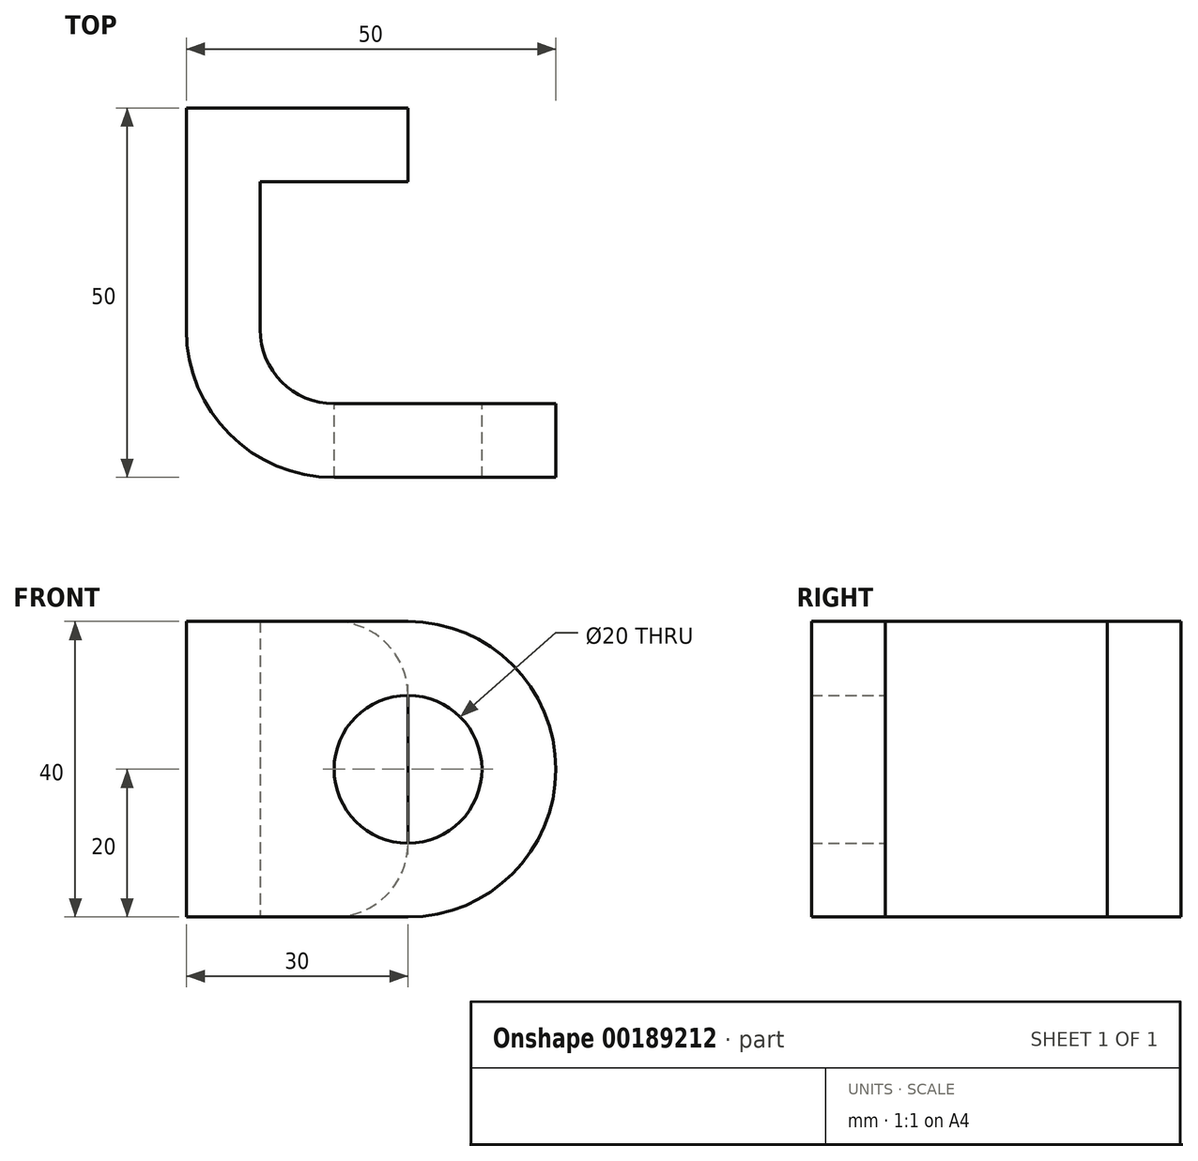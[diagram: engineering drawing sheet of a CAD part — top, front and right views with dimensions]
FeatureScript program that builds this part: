
annotation { "Feature Type Name" : "Feature", "Feature Type Description" : "" }
export const myFeature = defineFeature(function(context is Context, id is Id, definition is map)
    precondition{}
    {
        {
            var Q0;
            Q0=qCreatedBy(makeId("Top.planeOp"),FACE);
            var sketch = newSketch(context, id + "F0", { "sketchPlane" : qUnion([Q0])});
            skLineSegment(sketch, "E0", {"start": v(0, 10) * mm, "end": v(0, 30) * mm});
            skLineSegment(sketch, "E1", {"start": v(0, 30) * mm, "end": v(20, 30) * mm});
            skLineSegment(sketch, "E2", {"start": v(20, 30) * mm, "end": v(20, 40) * mm});
            skLineSegment(sketch, "E3", {"start": v(20, 40) * mm, "end": v(-10, 40) * mm});
            skLineSegment(sketch, "E4", {"start": v(-10, 40) * mm, "end": v(-10, 10) * mm});
            skLineSegment(sketch, "E5", {"start": v(10, -10) * mm, "end": v(40, -10) * mm});
            skLineSegment(sketch, "E6", {"start": v(40, -10) * mm, "end": v(40, 0) * mm});
            skLineSegment(sketch, "E7", {"start": v(40, 0) * mm, "end": v(10, 0) * mm});
            skPoint(sketch, "E8.visualSharp", {"position": v(0, 0) * mm});
            skArc(sketch, "E8.filletArc", {"start": v(0, 10) * mm, "mid": v(2.93, 2.93) * mm, "end": v(10, 0) * mm});
            skPoint(sketch, "E9.visualSharp", {"position": v(-10, -10) * mm});
            skArc(sketch, "E9.filletArc", {"start": v(-10, 10) * mm, "mid": v(-4.14, -4.14) * mm, "end": v(10, -10) * mm});
            skSolve(sketch);
        }
        {
            var Q0;
            Q0=makeQuery(id+"F0.imprint","IMPRINT",FACE,{"disambiguationData":[TD([[makeQuery(id+"F0.imprint","IMPRINT",EDGE,{"derivedFrom":sQuery(id+"F0.wireOp",EDGE,"E0")}),1.0]])]});
            extrude(context, id + "F1", {"entities" : qUnion([Q0]), "endBound" : BoundingType.SYMMETRIC, "depth" : 40 * mm});
        }
        {
            var Q0;
            Q0=makeQuery(id+"F1.opExtrude","CAP_EDGE",EDGE,{"disambiguationData":[OSD([sQuery(id+"F0.wireOp",EDGE,"E2")])],"isStart":false});
            var Q1;
            Q1=makeQuery(id+"F1.opExtrude","CAP_EDGE",EDGE,{"disambiguationData":[OSD([sQuery(id+"F0.wireOp",EDGE,"E2")])],"isStart":true});
            fillet(context, id + "F2", {"entities" : qUnion([Q0, Q1]), "radius" : 10 * mm, "tangentPropagation" : true, "allowEdgeOverflow" : false});
        }
        {
            var Q0;
            Q0=makeQuery(id+"F1.opExtrude","CAP_EDGE",EDGE,{"disambiguationData":[OSD([sQuery(id+"F0.wireOp",EDGE,"E6")])],"isStart":false});
            var Q1;
            Q1=makeQuery(id+"F1.opExtrude","CAP_EDGE",EDGE,{"disambiguationData":[OSD([sQuery(id+"F0.wireOp",EDGE,"E6")])],"isStart":true});
            fillet(context, id + "F3", {"entities" : qUnion([Q0, Q1]), "radius" : 20 * mm, "tangentPropagation" : true, "allowEdgeOverflow" : false});
        }
        {
            var Q0;
            Q0=makeQuery(id+"F1.opExtrude","SWEPT_FACE",FACE,{"disambiguationData":[OSD([sQuery(id+"F0.wireOp",EDGE,"E7")])]});
            var sketch = newSketch(context, id + "F4", { "sketchPlane" : qUnion([Q0])});
            skCircle(sketch, "E10", {"center": v(-20, 0) * mm, "radius": 10 * mm});
            skSolve(sketch);
        }
        {
            var Q0;
            Q0=makeQuery(id+"F4.imprint","IMPRINT",FACE,{"disambiguationData":[TD([[makeQuery(id+"F4.imprint","IMPRINT",EDGE,{"derivedFrom":sQuery(id+"F4.wireOp",EDGE,"E10")}),1.0]])]});
            extrude(context, id + "F5", {"entities" : qUnion([Q0]), "operationType" : NewBodyOperationType.REMOVE, "endBound" : BoundingType.THROUGH_ALL, "oppositeDirection" : true, "depth" : 25 * mm});
        }
    });
